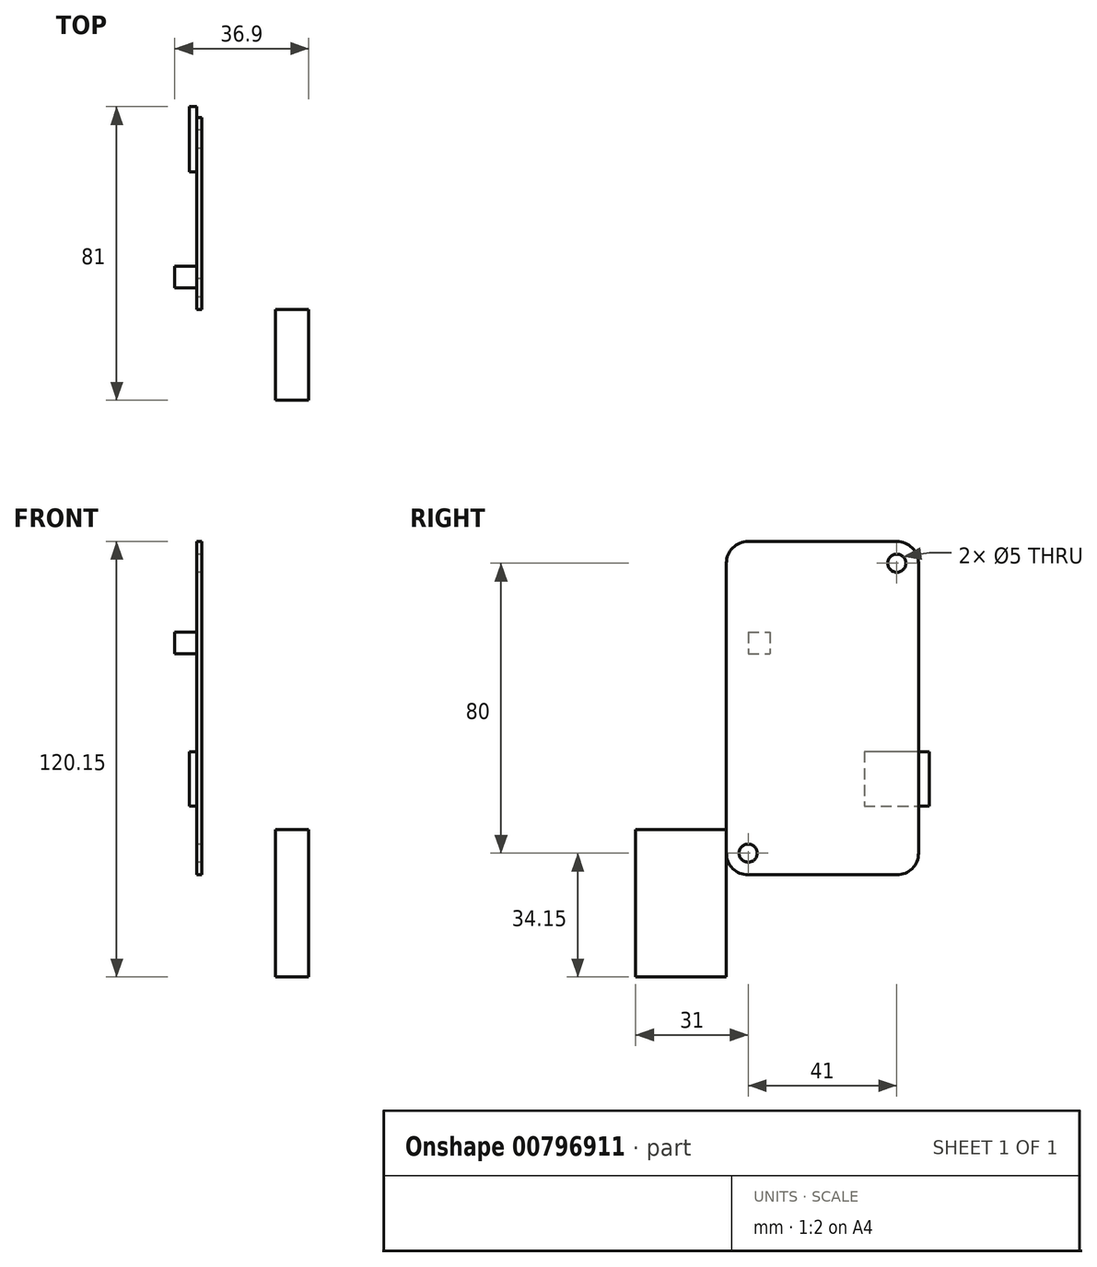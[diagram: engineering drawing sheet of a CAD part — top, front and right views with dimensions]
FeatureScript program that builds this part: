
annotation { "Feature Type Name" : "Feature", "Feature Type Description" : "" }
export const myFeature = defineFeature(function(context is Context, id is Id, definition is map)
    precondition{}
    {
        {
            var Q0;
            Q0=qCreatedBy(makeId("Right.planeOp"),FACE);
            var sketch = newSketch(context, id + "F0", { "sketchPlane" : qUnion([Q0])});
            skLineSegment(sketch, "E0.bottom", {"start": v(0, 0) * mm, "end": v(53, 0) * mm});
            skLineSegment(sketch, "E0.top", {"start": v(0, 92) * mm, "end": v(53, 92) * mm});
            skLineSegment(sketch, "E0.left", {"start": v(0, 0) * mm, "end": v(0, 92) * mm});
            skLineSegment(sketch, "E0.right", {"start": v(53, 0) * mm, "end": v(53, 92) * mm});
            skCircle(sketch, "E1", {"center": v(6, 6) * mm, "radius": 2.5 * mm});
            skCircle(sketch, "E2", {"center": v(47, 86) * mm, "radius": 2.5 * mm});
            skSolve(sketch);
        }
        {
            var Q0;
            Q0=makeQuery(id+"F0.imprint","IMPRINT",FACE,{"disambiguationData":[TD([[makeQuery(id+"F0.imprint","IMPRINT",EDGE,{"derivedFrom":sQuery(id+"F0.wireOp",EDGE,"E0.bottom")}),1.0]])]});
            extrude(context, id + "F1", {"entities" : qUnion([Q0]), "depth" : 1.5 * mm, "offsetDistance" : 25 * mm});
        }
        {
            var Q0;
            Q0=makeQuery(id+"F1.opExtrude","SWEPT_EDGE",EDGE,{"disambiguationData":[OSD([sQuery(id+"F0.wireOp",EDGE,"E0.top"),sQuery(id+"F0.wireOp",EDGE,"E0.left")])]});
            var Q1;
            Q1=makeQuery(id+"F1.opExtrude","SWEPT_EDGE",EDGE,{"disambiguationData":[OSD([sQuery(id+"F0.wireOp",EDGE,"E0.top"),sQuery(id+"F0.wireOp",EDGE,"E0.right")])]});
            var Q2;
            Q2=makeQuery(id+"F1.opExtrude","SWEPT_EDGE",EDGE,{"disambiguationData":[OSD([sQuery(id+"F0.wireOp",EDGE,"E0.bottom"),sQuery(id+"F0.wireOp",EDGE,"E0.right")])]});
            var Q3;
            Q3=makeQuery(id+"F1.opExtrude","SWEPT_EDGE",EDGE,{"disambiguationData":[OSD([sQuery(id+"F0.wireOp",EDGE,"E0.bottom"),sQuery(id+"F0.wireOp",EDGE,"E0.left")])]});
            fillet(context, id + "F2", {"entities" : qUnion([Q0, Q1, Q2, Q3]), "radius" : 6 * mm, "tangentPropagation" : true, "allowEdgeOverflow" : false});
        }
        {
            var Q0;
            Q0=makeQuery(id+"F1.opExtrude","CAP_FACE",FACE,{"disambiguationData":[OSD([sQuery(id+"F0.wireOp",EDGE,"E0.bottom"),sQuery(id+"F0.wireOp",EDGE,"E0.top"),sQuery(id+"F0.wireOp",EDGE,"E0.left"),sQuery(id+"F0.wireOp",EDGE,"E0.right"),sQuery(id+"F0.wireOp",EDGE,"E1"),sQuery(id+"F0.wireOp",EDGE,"E2")])],"isStart":true});
            var sketch = newSketch(context, id + "F3", { "sketchPlane" : qUnion([Q0])});
            skLineSegment(sketch, "E3.bottom", {"start": v(-6, 67) * mm, "end": v(-12, 67) * mm});
            skLineSegment(sketch, "E3.top", {"start": v(-6, 61) * mm, "end": v(-12, 61) * mm});
            skLineSegment(sketch, "E3.left", {"start": v(-6, 67) * mm, "end": v(-6, 61) * mm});
            skLineSegment(sketch, "E3.right", {"start": v(-12, 67) * mm, "end": v(-12, 61) * mm});
            skSolve(sketch);
        }
        {
            var Q0;
            Q0=makeQuery(id+"F3.imprint","IMPRINT",FACE,{"disambiguationData":[TD([[makeQuery(id+"F3.imprint","IMPRINT",EDGE,{"derivedFrom":sQuery(id+"F3.wireOp",EDGE,"E3.bottom")}),1.0]])]});
            extrude(context, id + "F4", {"entities" : qUnion([Q0]), "operationType" : NewBodyOperationType.ADD, "depth" : 6 * mm, "offsetDistance" : 25 * mm});
        }
        {
            var Q0;
            Q0=makeQuery(id+"F1.opExtrude","CAP_FACE",FACE,{"disambiguationData":[OSD([sQuery(id+"F0.wireOp",EDGE,"E0.bottom"),sQuery(id+"F0.wireOp",EDGE,"E0.top"),sQuery(id+"F0.wireOp",EDGE,"E0.left"),sQuery(id+"F0.wireOp",EDGE,"E0.right"),sQuery(id+"F0.wireOp",EDGE,"E1"),sQuery(id+"F0.wireOp",EDGE,"E2")])],"isStart":true});
            var sketch = newSketch(context, id + "F5", { "sketchPlane" : qUnion([Q0])});
            skLineSegment(sketch, "E4", {"start": v(-38, 34) * mm, "end": v(-38, 19) * mm});
            skLineSegment(sketch, "E5", {"start": v(-38, 19) * mm, "end": v(-56, 19) * mm});
            skLineSegment(sketch, "E6", {"start": v(-56, 19) * mm, "end": v(-56, 34) * mm});
            skLineSegment(sketch, "E7", {"start": v(-56, 34) * mm, "end": v(-38, 34) * mm});
            skSolve(sketch);
        }
        {
            var Q0;
            {var subQ0=sQuery(id+"F5.wireOp",EDGE,"E6");Q0=makeQuery(id+"F5.imprint","IMPRINT",FACE,{"disambiguationData":[TD([[makeQuery(id+"F5.imprint","IMPRINT",EDGE,{"derivedFrom":subQ0}),-1.0]])]});}
            var Q1;
            {var subQ0=sQuery(id+"F5.wireOp",EDGE,"E4");Q1=makeQuery(id+"F5.imprint","IMPRINT",FACE,{"disambiguationData":[TD([[makeQuery(id+"F5.imprint","IMPRINT",EDGE,{"derivedFrom":subQ0}),-1.0]])]});}
            extrude(context, id + "F6", {"entities" : qUnion([Q0, Q1]), "depth" : 2 * mm, "offsetDistance" : 25 * mm});
        }
        {
            var Q0;
            Q0=qCreatedBy(makeId("Front.planeOp"),FACE);
            var sketch = newSketch(context, id + "F7", { "sketchPlane" : qUnion([Q0])});
            skLineSegment(sketch, "E8.bottom", {"start": v(21.8, -28.15) * mm, "end": v(30.9, -28.15) * mm});
            skLineSegment(sketch, "E8.top", {"start": v(21.8, 12.57) * mm, "end": v(30.9, 12.57) * mm});
            skLineSegment(sketch, "E8.left", {"start": v(21.8, -28.15) * mm, "end": v(21.8, 12.57) * mm});
            skLineSegment(sketch, "E8.right", {"start": v(30.9, -28.15) * mm, "end": v(30.9, 12.57) * mm});
            skSolve(sketch);
        }
        {
            var Q0;
            Q0 = qSketchRegion(id + "F7", true);
            extrude(context, id + "F8", {"entities" : qUnion([Q0]), "depth" : 25 * mm, "offsetDistance" : 25 * mm});
        }
    });
